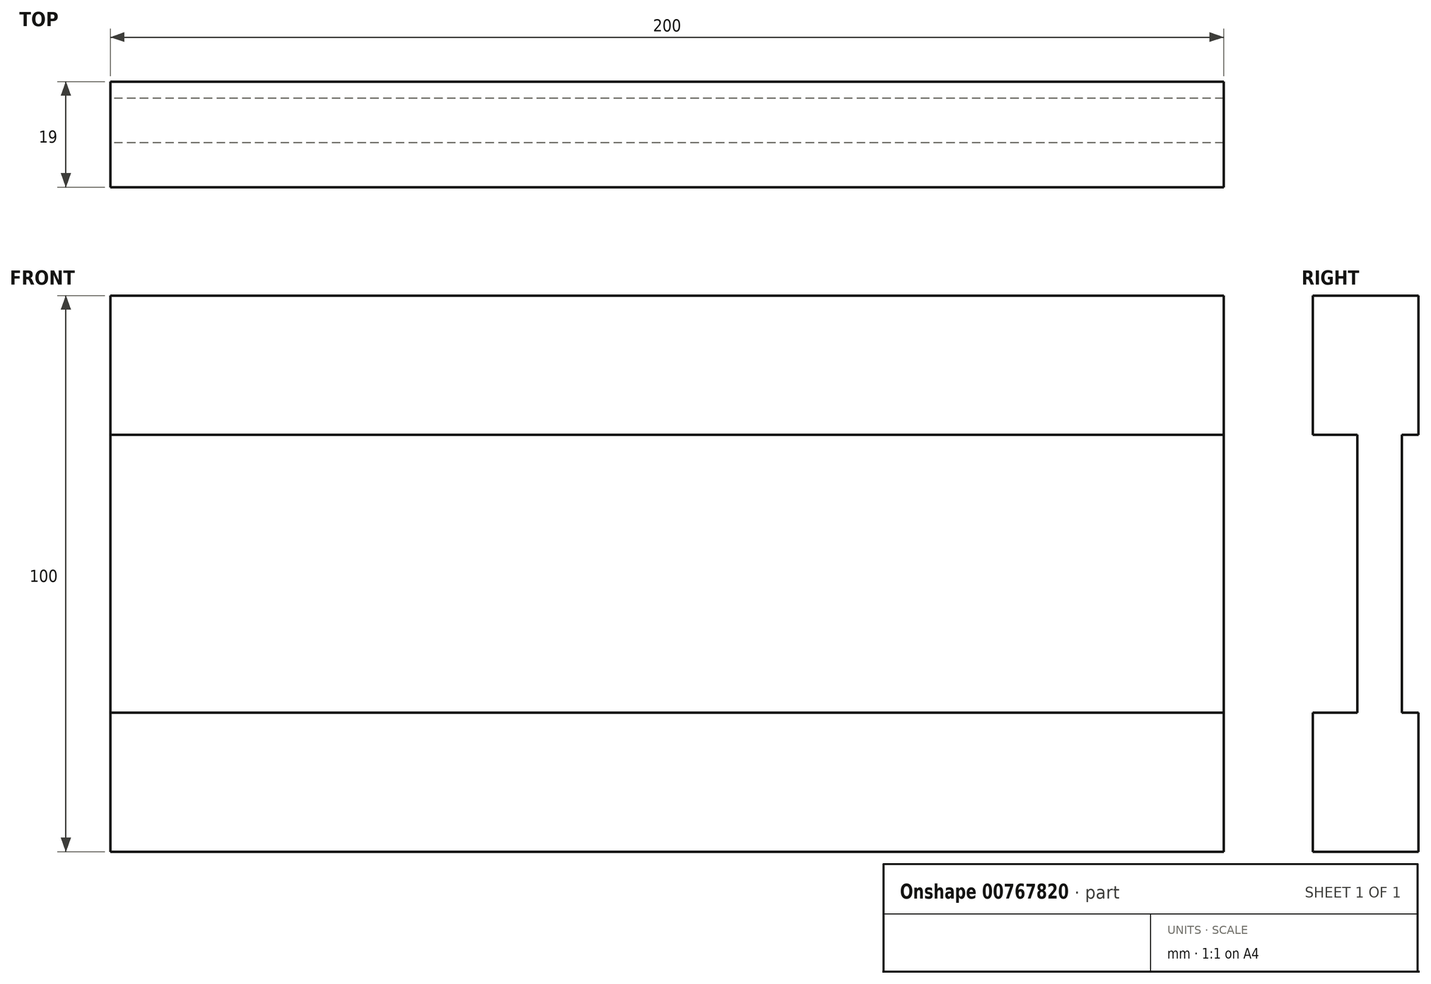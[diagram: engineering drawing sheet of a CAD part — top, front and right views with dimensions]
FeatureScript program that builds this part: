
annotation { "Feature Type Name" : "Feature", "Feature Type Description" : "" }
export const myFeature = defineFeature(function(context is Context, id is Id, definition is map)
    precondition{}
    {
        {
            var Q0;
            Q0=qCreatedBy(makeId("Right.planeOp"),FACE);
            var sketch = newSketch(context, id + "F0", { "sketchPlane" : qUnion([Q0])});
            skLineSegment(sketch, "E0.bottom", {"start": v(0, 50) * mm, "end": v(-19, 50) * mm});
            skLineSegment(sketch, "E0.top", {"start": v(0, -50) * mm, "end": v(-19, -50) * mm});
            skLineSegment(sketch, "E0.left", {"start": v(0, 50) * mm, "end": v(0, 25) * mm});
            skLineSegment(sketch, "E0.right", {"start": v(-19, 50) * mm, "end": v(-19, 25) * mm});
            skLineSegment(sketch, "E1.bottom", {"start": v(0, 25) * mm, "end": v(-3, 25) * mm});
            skLineSegment(sketch, "E1.top", {"start": v(0, -25) * mm, "end": v(-3, -25) * mm});
            skLineSegment(sketch, "E1.right", {"start": v(-3, 25) * mm, "end": v(-3, -25) * mm});
            skLineSegment(sketch, "E2.trimOffspring", {"start": v(0, -25) * mm, "end": v(0, -50) * mm});
            skPoint(sketch, "E3", {"position": v(-3, 0) * mm});
            skLineSegment(sketch, "E4.bottom", {"start": v(-19, 25) * mm, "end": v(-11, 25) * mm});
            skLineSegment(sketch, "E4.top", {"start": v(-19, -25) * mm, "end": v(-11, -25) * mm});
            skLineSegment(sketch, "E4.right", {"start": v(-11, 25) * mm, "end": v(-11, -25) * mm});
            skPoint(sketch, "E5", {"position": v(-11, 0) * mm});
            skLineSegment(sketch, "E6.trimOffspring", {"start": v(-19, -25) * mm, "end": v(-19, -50) * mm});
            skSolve(sketch);
        }
        {
            var Q0;
            Q0=makeQuery(id+"F0.imprint","IMPRINT",FACE,{"disambiguationData":[TD([[makeQuery(id+"F0.imprint","IMPRINT",EDGE,{"derivedFrom":sQuery(id+"F0.wireOp",EDGE,"E0.bottom")}),1.0]])]});
            extrude(context, id + "F1", {"entities" : qUnion([Q0]), "depth" : 200 * mm, "offsetDistance" : 25 * mm});
        }
    });
